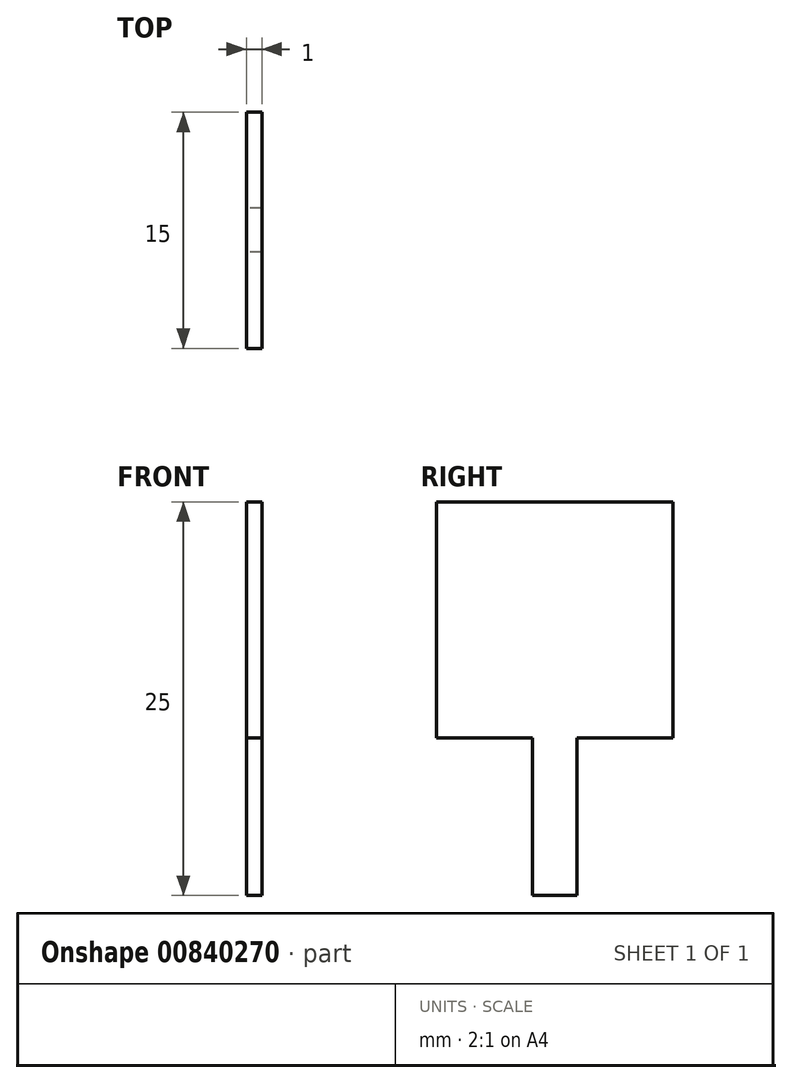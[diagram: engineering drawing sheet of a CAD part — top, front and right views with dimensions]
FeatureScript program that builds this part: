
annotation { "Feature Type Name" : "Feature", "Feature Type Description" : "" }
export const myFeature = defineFeature(function(context is Context, id is Id, definition is map)
    precondition{}
    {
        {
            var Q0;
            Q0=qCreatedBy(makeId("Right.planeOp"),FACE);
            var sketch = newSketch(context, id + "F0", { "sketchPlane" : qUnion([Q0])});
            skLineSegment(sketch, "E0.bottom", {"start": v(0, 0) * mm, "end": v(11.5, 0) * mm});
            skLineSegment(sketch, "E0.top", {"start": v(0, -15) * mm, "end": v(4.35, -15) * mm});
            skLineSegment(sketch, "E1", {"start": v(5.25, -25) * mm, "end": v(6.25, -25) * mm});
            skLineSegment(sketch, "E2.trimOffspring", {"start": v(7.15, -15) * mm, "end": v(11.5, -15) * mm});
            skLineSegment(sketch, "E3.0", {"start": v(-1.75, 0) * mm, "end": v(-1.75, -15) * mm});
            skLineSegment(sketch, "E4.0", {"start": v(13.25, 0) * mm, "end": v(13.25, -15) * mm});
            skLineSegment(sketch, "E5", {"start": v(-1.75, 0) * mm, "end": v(13.25, 0) * mm});
            skLineSegment(sketch, "E6", {"start": v(13.25, -15) * mm, "end": v(7.15, -15) * mm});
            skLineSegment(sketch, "E7.0", {"start": v(4.35, -15) * mm, "end": v(4.35, -25) * mm});
            skLineSegment(sketch, "E8.0", {"start": v(7.15, -15) * mm, "end": v(7.15, -25) * mm});
            skLineSegment(sketch, "E9", {"start": v(4.35, -25) * mm, "end": v(7.15, -25) * mm});
            skPoint(sketch, "E10.end.orphan", {"position": v(5.75, -25) * mm});
            skPoint(sketch, "E10.start.orphan", {"position": v(5.75, -15) * mm});
            skLineSegment(sketch, "E11.trimOffspring", {"start": v(4.35, -15) * mm, "end": v(-1.75, -15) * mm});
            skSolve(sketch);
        }
        {
            var Q0;
            Q0=makeQuery(id+"F0.imprint","IMPRINT",FACE,{"disambiguationData":[TD([[makeQuery(id+"F0.imprint","IMPRINT",EDGE,{"derivedFrom":sQuery(id+"F0.wireOp",EDGE,"E0.bottom")}),-1.0]])]});
            var Q1;
            Q1=makeQuery(id+"F0.imprint","IMPRINT",FACE,{"disambiguationData":[TD([[makeQuery(id+"F0.imprint","IMPRINT",EDGE,{"derivedFrom":sQuery(id+"F0.wireOp",EDGE,"qPRy3xUT-NRqM-xTn5-TbLo-p4iQvefC5ACk")}),-1.0]])]});
            var Q2;
            {var subQ3=sQuery(id+"F0.wireOp",EDGE,"63f1d356-c40f-4f39-ade3-4e022c9102be.0");Q2=makeQuery(id+"F0.imprint","IMPRINT",FACE,{"disambiguationData":[TD([[makeQuery(id+"F0.imprint","IMPRINT",EDGE,{"derivedFrom":subQ3}),1.0]])]});}
            var Q3;
            {var subQ3=sQuery(id+"F0.wireOp",EDGE,"E3.0");Q3=makeQuery(id+"F0.imprint","IMPRINT",FACE,{"disambiguationData":[TD([[makeQuery(id+"F0.imprint","IMPRINT",EDGE,{"derivedFrom":subQ3}),1.0]])]});}
            var Q4;
            {var subQ0=sQuery(id+"F0.wireOp",EDGE,"5dc07093-3f57-4306-a93b-4e72212c7467.0");Q4=makeQuery(id+"F0.imprint","IMPRINT",FACE,{"disambiguationData":[TD([[makeQuery(id+"F0.imprint","IMPRINT",EDGE,{"derivedFrom":subQ0}),1.0]])]});}
            var Q5;
            {var subQ0=sQuery(id+"F0.wireOp",EDGE,"51NmYdBp-mA1z-wu9Q-53MT-rEDAkP0LJ8wn");Q5=makeQuery(id+"F0.imprint","IMPRINT",FACE,{"disambiguationData":[TD([[makeQuery(id+"F0.imprint","IMPRINT",EDGE,{"derivedFrom":subQ0}),-1.0]])]});}
            extrude(context, id + "F1", {"entities" : qUnion([Q0, Q1, Q2, Q3, Q4, Q5]), "depth" : 1 * mm, "offsetDistance" : 25 * mm});
        }
    });
